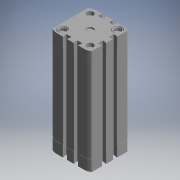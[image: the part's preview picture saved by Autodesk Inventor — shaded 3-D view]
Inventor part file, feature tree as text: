
AUTODESK INVENTOR PART (.ipt)
format: ipt  version: 2017.3 (Build 213256000, 256)  size: 790,528 bytes
history: native  units: mm (DEFAULTED — no unit token found)
features: other x84, sketch x30, revolve x13, hole x11, thread x8, extrude x6
ambient origin geometry x8: Origin, YZ Plane, XZ Plane, XY Plane, X Axis, Y Axis, Z Axis, Center Point
bodies: Solid1 (feature_tree)
feature tree (152):
  extrude  "Extrusion1"  Depth=115.0mm TaperAngle=0.0deg
  extrude  "Extrusion2"  TaperAngle=360.0deg  [1 undecoded]
  hole  "Hole1"  [1 undecoded]
  hole  "Hole2"  [1 undecoded]
  revolve  "Revolution1"  Angle=360.0deg
  hole  "Hole3"  [1 undecoded]
  hole  "Hole4"  [1 undecoded]
  revolve  "Revolution2"  Angle=360.0deg
  thread  "Thread1"  [1 undecoded]
  hole  "Hole5"  [1 undecoded]
  revolve  "Revolution3"  Angle=360.0deg
  thread  "Thread2"  [1 undecoded]
  hole  "Hole6"  [1 undecoded]
  hole  "Hole7"  [1 undecoded]
  revolve  "Revolution4"  [1 undecoded]
  thread  "Thread3"  [1 undecoded]
  revolve  "Revolution5"  [1 undecoded]
  thread  "Thread4"  [1 undecoded]
  revolve  "Revolution6"  [1 undecoded]
  thread  "Thread5"  [1 undecoded]
  revolve  "Revolution7"  [1 undecoded]
  hole  "Hole8"  [1 undecoded]
  revolve  "Revolution8"  [1 undecoded]
  thread  "Thread6"  [1 undecoded]
  revolve  "Revolution9"  [1 undecoded]
  hole  "Hole9"  [1 undecoded]
  revolve  "Revolution10"  [1 undecoded]
  thread  "Thread7"  [1 undecoded]
  revolve  "Revolution11"  [1 undecoded]
  hole  "Hole10"  [1 undecoded]
  revolve  "Revolution12"  [1 undecoded]
  thread  "Thread8"  [1 undecoded]
  revolve  "Revolution13"  [1 undecoded]
  hole  "Hole11"  [1 undecoded]
  extrude  "Extrusion3"  [1 undecoded]
  extrude  "Extrusion4"  [1 undecoded]
  extrude  "Extrusion5"  [1 undecoded]
  extrude  "Extrusion6"  [1 undecoded]
  other  "CYLINDER_XY"
  other  "CYLINDER_YZ"
  other  "CYLINDER_ZX"
  other  "CYLINDER_X"
  other  "CYLINDER_Y"
  other  "CYLINDER_Z"
  other  "CYLINDER_Center"
  other  "FDT_FRONT_XY"
  other  "FDT_FRONT_YZ"
  other  "FDT_FRONT_ZX"
  other  "FDT_FRONT_X"
  other  "FDT_FRONT_Y"
  other  "FDT_FRONT_Z"
  other  "FDT_FRONT_Center"
  other  "FDT_QSFRONT_XY"
  other  "FDT_QSFRONT_YZ"
  other  "FDT_QSFRONT_ZX"
  other  "FDT_QSFRONT_X"
  other  "FDT_QSFRONT_Y"
  other  "FDT_QSFRONT_Z"
  other  "FDT_QSFRONT_Center"
  other  "FDT_QSREAR_XY"
  other  "FDT_QSREAR_YZ"
  other  "FDT_QSREAR_ZX"
  other  "FDT_QSREAR_X"
  other  "FDT_QSREAR_Y"
  other  "FDT_QSREAR_Z"
  other  "FDT_QSREAR_Center"
  other  "FDT_REAR_XY"
  other  "FDT_REAR_YZ"
  other  "FDT_REAR_ZX"
  other  "FDT_REAR_X"
  other  "FDT_REAR_Y"
  other  "FDT_REAR_Z"
  other  "FDT_REAR_Center"
  other  "FDT_SLOT3_XY"
  other  "FDT_SLOT3_YZ"
  other  "FDT_SLOT3_ZX"
  other  "FDT_SLOT3_X"
  other  "FDT_SLOT3_Y"
  other  "FDT_SLOT3_Z"
  other  "FDT_SLOT3_Center"
  other  "FDT_SLOT4_XY"
  other  "FDT_SLOT4_YZ"
  other  "FDT_SLOT4_ZX"
  other  "FDT_SLOT4_X"
  other  "FDT_SLOT4_Y"
  other  "FDT_SLOT4_Z"
  other  "FDT_SLOT4_Center"
  other  "FDT_SLOT5_XY"
  other  "FDT_SLOT5_YZ"
  other  "FDT_SLOT5_ZX"
  other  "FDT_SLOT5_X"
  other  "FDT_SLOT5_Y"
  other  "FDT_SLOT5_Z"
  other  "FDT_SLOT5_Center"
  other  "FDT_SLOT6_XY"
  other  "FDT_SLOT6_YZ"
  other  "FDT_SLOT6_ZX"
  other  "FDT_SLOT6_X"
  other  "FDT_SLOT6_Y"
  other  "FDT_SLOT6_Z"
  other  "FDT_SLOT6_Center"
  other  "FDT_SLOT7_XY"
  other  "FDT_SLOT7_YZ"
  other  "FDT_SLOT7_ZX"
  other  "FDT_SLOT7_X"
  other  "FDT_SLOT7_Y"
  other  "FDT_SLOT7_Z"
  other  "FDT_SLOT7_Center"
  other  "FDT_SLOT8_XY"
  other  "FDT_SLOT8_YZ"
  other  "FDT_SLOT8_ZX"
  other  "FDT_SLOT8_X"
  other  "FDT_SLOT8_Y"
  other  "FDT_SLOT8_Z"
  other  "FDT_SLOT8_Center"
  other  "TO_DUMMY_XY"
  other  "TO_DUMMY_YZ"
  other  "TO_DUMMY_ZX"
  other  "TO_DUMMY_X"
  other  "TO_DUMMY_Y"
  other  "TO_DUMMY_Z"
  other  "TO_DUMMY_Center"
  sketch  "Skizze_2"  dims[d0=145.0mm d1=0.0mm d2=115.0mm d3=0.0mm]
  sketch  "Sketch_113"
  sketch  "Sketch3"  dims[d4=8.566mm d5=8.581mm d6=9.728mm d7=2.0mm d8=90.0deg d9=12.5mm d10=0.0mm]
  sketch  "Sketch4"  dims[d19=9.0mm d20=6.0mm d21=4.0mm d22=2.0mm d23=90.0deg d24=2.1mm d25=0.0mm]
  sketch  "Skizze_5"  dims[d34=20.8585mm d35=0.0mm]
  sketch  "Sketch6"  dims[d36=9.0mm d37=6.0mm d38=12.8mm d39=7.0mm d40=90.0deg d41=26.0mm d42=0.0mm d43=360.0deg]
  sketch  "Sketch7"  dims[d44=20.8585mm d45=0.0mm]
  sketch  "Sketch_27"  dims[d118=0.0mm d119=0.0mm d120=0.0mm d121=0.0mm d122=0.0mm d123=0.0mm d124=0.0mm d125=0.0mm d126=0.0mm d127=0.0mm d128=0.0mm d129=0.0mm]
  sketch  "Sketch9"  dims[d61=20.8585mm d62=0.0mm d63=360.0deg]
  sketch  "Sketch_28"
  sketch  "Sketch11"  dims[d70=6.0mm d71=6.0mm d72=4.0mm d73=2.0mm d74=90.0deg d75=104.0mm d76=0.0mm d77=360.0deg]
  sketch  "Sketch12"  dims[d78=9.4585mm d79=0.0mm d80=360.0deg]
  sketch  "Sketch_29"
  sketch  "Sketch_30"
  sketch  "Skizze_12"  dims[d81=6.0mm d82=6.0mm d83=4.0mm d84=2.0mm d85=90.0deg d86=104.0mm d87=0.0mm d88=360.0deg d89=9.4585mm d90=0.0mm]
  sketch  "Sketch_123"
  sketch  "Sketch17"  dims[d92=6.0mm d93=6.0mm d94=4.0mm d95=2.0mm d96=90.0deg d97=104.0mm d98=0.0mm d99=360.0deg]
  sketch  "Sketch_3"  dims[d11=8.566mm d12=8.581mm d13=9.728mm d14=2.0mm d15=90.0deg d16=12.5mm d17=0.0mm d18=360.0deg]
  sketch  "Sketch_117"
  sketch  "Sketch20"  dims[d100=9.4585mm d101=0.0mm d102=360.0deg]
  sketch  "Skizze_13"  dims[d91=360.0deg]
  sketch  "Sketch_121"
  sketch  "Sketch23"  dims[d103=6.0mm d104=6.0mm d105=4.0mm d106=2.0mm d107=90.0deg d108=104.0mm d109=0.0mm d110=4.4mm d111=0.0mm d112=4.4mm d113=0.0mm]
  sketch  "Sketch_4"  dims[d26=9.0mm d27=6.0mm d28=12.8mm d29=7.0mm d30=90.0deg d31=26.0mm d32=0.0mm d33=360.0deg]
  sketch  "Sketch_118"
  sketch  "Sketch26"  dims[d114=4.4mm d115=0.0mm d116=4.4mm d117=0.0mm]
  sketch  "Sketch_8"  dims[d53=9.0mm d54=6.0mm d55=12.8mm d56=7.0mm d57=90.0deg d58=26.0mm d59=0.0mm d60=360.0deg]
  sketch  "Sketch_7"  dims[d46=9.0mm d47=6.0mm d48=12.8mm d49=7.0mm d50=90.0deg d51=26.0mm d52=0.0mm]
  sketch  "Sketch_9"  dims[d64=20.8585mm d65=0.0mm d66=360.0deg]
  sketch  "Sketch_10"  dims[d67=9.4585mm d68=0.0mm d69=360.0deg]
note: 34 required parameter values undecoded (feature->parameter linkage not recoverable at this tier; creation-order binding heuristic only, values carry confidence <= 0.55)